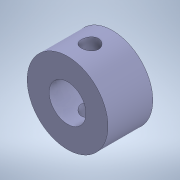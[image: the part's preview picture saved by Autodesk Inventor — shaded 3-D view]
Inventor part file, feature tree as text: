
AUTODESK INVENTOR PART (.ipt)
format: ipt  version: 2021 (Build 250183000, 183)  size: 119,296 bytes
history: native  units: mm
features: extrude x2, sketch x2
ambient origin geometry x8: Origin, YZ Plane, XZ Plane, XY Plane, X Axis, Y Axis, Z Axis, Center Point
bodies: Solid1 (feature_tree)
feature tree (4):
  extrude  "Extrusion1"  Depth=18.0mm
  extrude  "Extrusion2"  Depth=10.0mm
  sketch  "Sketch1"  dims[d0=8.2mm d1=18.0mm]
  sketch  "Sketch2"  dims[d2=10.0mm d3=0.0mm d4=3.8mm d5=11.0mm d6=11.0mm d7=0.0mm d8=0.0mm]
